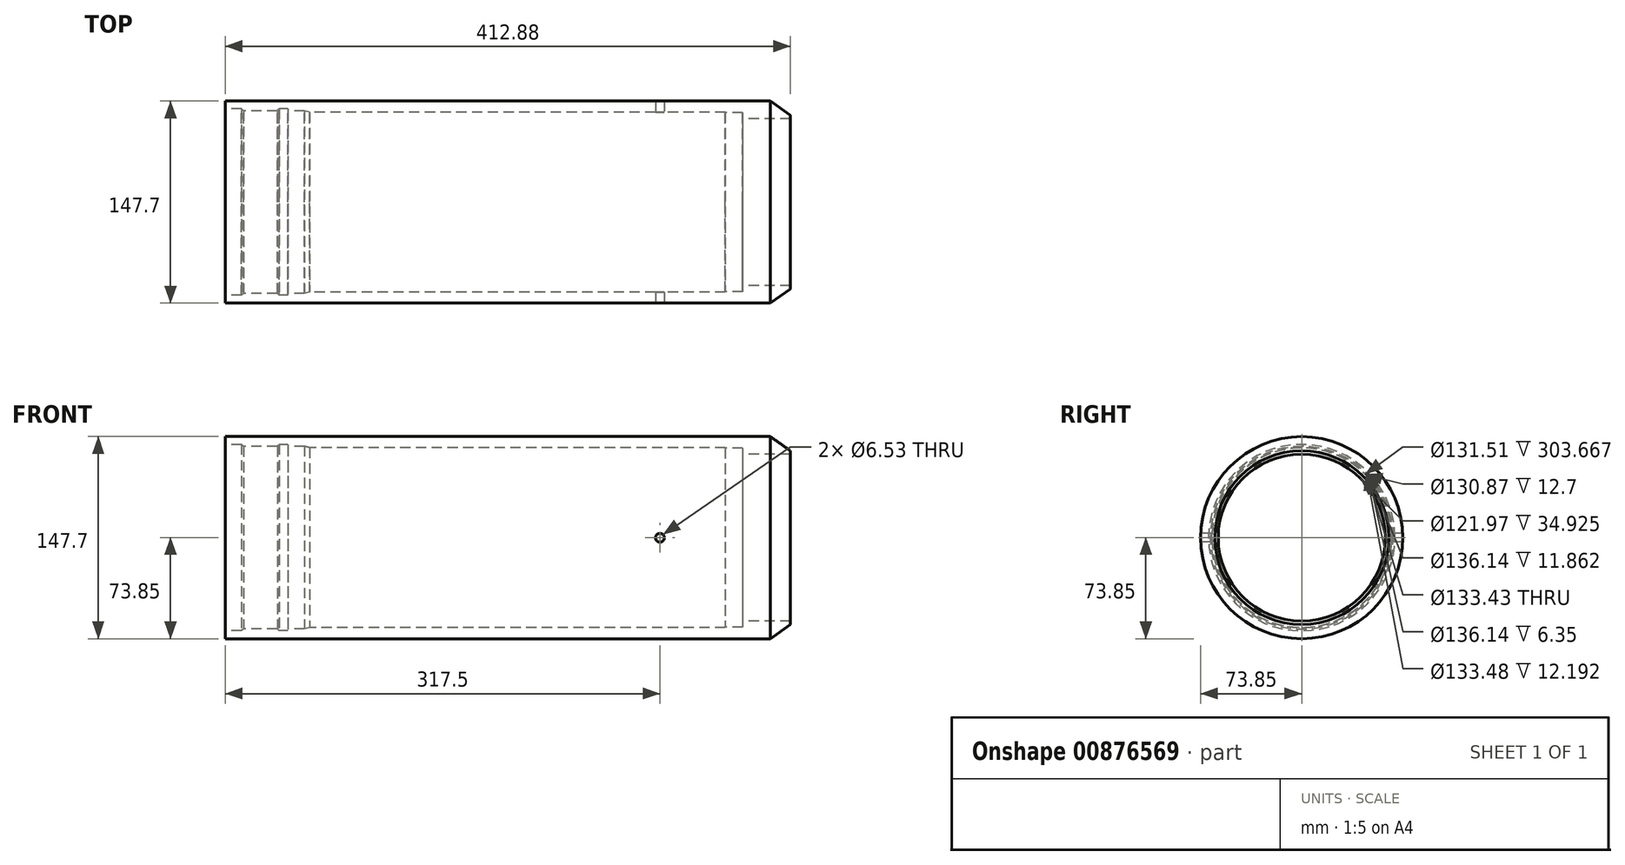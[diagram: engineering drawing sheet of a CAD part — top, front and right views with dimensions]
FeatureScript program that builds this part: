
annotation { "Feature Type Name" : "Feature", "Feature Type Description" : "" }
export const myFeature = defineFeature(function(context is Context, id is Id, definition is map)
    precondition{}
    {
        {
            var Q0;
            Q0=qCreatedBy(makeId("Front.planeOp"),FACE);
            var sketch = newSketch(context, id + "F0", { "sketchPlane" : qUnion([Q0])});
            skLineSegment(sketch, "E0", {"start": v(0, 0) * mm, "end": v(412.88, 0) * mm, "construction": true});
            skLineSegment(sketch, "E1", {"start": v(0, 68.07) * mm, "end": v(0, 73.85) * mm});
            skLineSegment(sketch, "E2", {"start": v(0, 73.85) * mm, "end": v(398.1, 73.85) * mm});
            skLineSegment(sketch, "E3", {"start": v(412.88, 63.5) * mm, "end": v(412.88, 60.99) * mm});
            skLineSegment(sketch, "E4", {"start": v(412.88, 60.99) * mm, "end": v(377.95, 60.99) * mm});
            skLineSegment(sketch, "E5", {"start": v(377.95, 60.99) * mm, "end": v(377.95, 65.44) * mm});
            skLineSegment(sketch, "E6", {"start": v(377.95, 65.44) * mm, "end": v(365.25, 65.44) * mm});
            skLineSegment(sketch, "E7", {"start": v(365.25, 65.75) * mm, "end": v(365.25, 65.44) * mm});
            skLineSegment(sketch, "E8", {"start": v(365.25, 65.75) * mm, "end": v(61.59, 65.75) * mm});
            skLineSegment(sketch, "E9", {"start": v(57.91, 66.74) * mm, "end": v(45.72, 66.74) * mm});
            skLineSegment(sketch, "E10", {"start": v(57.91, 66.74) * mm, "end": v(61.59, 65.75) * mm});
            skLineSegment(sketch, "E11", {"start": v(38.01, 66.71) * mm, "end": v(13.22, 66.71) * mm});
            skLineSegment(sketch, "E12", {"start": v(45.72, 66.74) * mm, "end": v(45.72, 68.07) * mm});
            skLineSegment(sketch, "E13", {"start": v(45.72, 68.07) * mm, "end": v(39.37, 68.07) * mm});
            skLineSegment(sketch, "E14", {"start": v(39.37, 68.07) * mm, "end": v(38.01, 66.71) * mm});
            skLineSegment(sketch, "E15", {"start": v(0, 68.07) * mm, "end": v(11.86, 68.07) * mm});
            skLineSegment(sketch, "E16", {"start": v(11.86, 68.07) * mm, "end": v(13.22, 66.71) * mm});
            skPoint(sketch, "E17.orphan", {"position": v(412.88, 63.5) * mm});
            skLineSegment(sketch, "E18", {"start": v(412.88, 63.5) * mm, "end": v(398.1, 73.85) * mm});
            skPoint(sketch, "E19.orphan", {"position": v(412.88, 73.85) * mm});
            skSolve(sketch);
        }
        {
            var Q0;
            Q0 = qSketchRegion(id + "F0", true);
            var Q1;
            Q1=sQuery(id+"F0.wireOp",EDGE,"E0");
            revolve(context, id + "F1", {"surfaceOperationType" : NewSurfaceOperationType.NEW, "entities" : qUnion([Q0]), "axis" : qUnion([Q1]), "revolveType" : RevolveType.FULL});
        }
        {
            var Q0;
            Q0=qCreatedBy(makeId("Front.planeOp"),FACE);
            var sketch = newSketch(context, id + "F2", { "sketchPlane" : qUnion([Q0])});
            skCircle(sketch, "E20", {"center": v(317.5, 0) * mm, "radius": 3.26 * mm});
            skSolve(sketch);
        }
        {
            var Q0;
            Q0 = qSketchRegion(id + "F2", true);
            extrude(context, id + "F3", {"entities" : qUnion([Q0]), "operationType" : NewBodyOperationType.REMOVE, "endBound" : BoundingType.SYMMETRIC, "oppositeDirection" : true, "depth" : 152.4 * mm, "offsetDistance" : 25.4 * mm});
        }
    });
